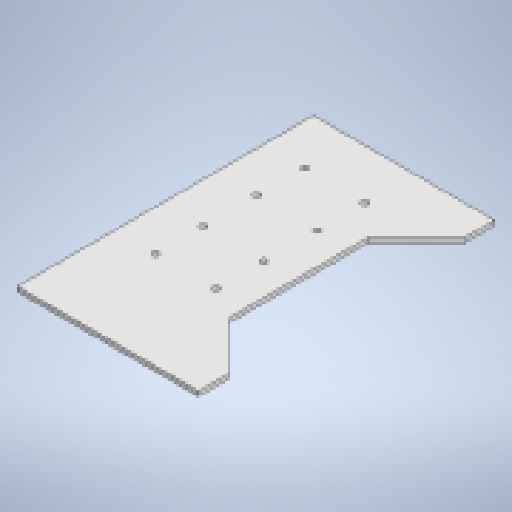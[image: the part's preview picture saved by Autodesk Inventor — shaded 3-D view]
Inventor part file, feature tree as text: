
AUTODESK INVENTOR PART (.ipt)
format: ipt  version: 2025.1 (Build 291241000, 241)  size: 381,952 bytes
history: native  units: mm
features: other x5, extrude x4, sketch x4, reference x4, fillet x2, projected_geometry x1
ambient origin geometry x8: Origin, YZ Plane, XZ Plane, XY Plane, X Axis, Y Axis, Z Axis, Center Point
bodies: Body1 (feature_tree)
feature tree (20):
  other  "ソリッド1"
  extrude  "押し出し1"  Depth=98.0mm
  extrude  "押し出し2"  Depth=60.0mm
  fillet  "フィレット1"  Radius=10.0mm
  extrude  "押し出し3"  Depth=2.0mm TaperAngle=0.0deg
  extrude  "押し出し4"  Depth=44.0mm
  fillet  "フィレット2"  Radius=2.2mm
  sketch  "スケッチ1"
  sketch  "スケッチ2"
  reference  "参照1"
  reference  "参照2"
  reference  "参照3"
  reference  "参照4"
  sketch  "スケッチ3"
  projected_geometry  "投影ループ1"
  sketch  "スケッチ4"
  other  "<userpath>\Documents\Inventor\Vixen\doutai.iam"
  other  "doutai.iam"
  other  "asikubi_asi:1"
  other  "asikubi_asi:2"
